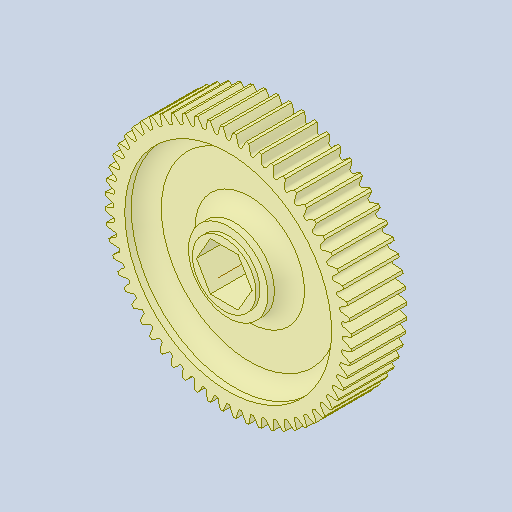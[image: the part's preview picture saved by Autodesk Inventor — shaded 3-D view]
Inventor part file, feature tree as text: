
AUTODESK INVENTOR PART (.ipt)
format: ipt  version: 2022.3 (Build 263350000, 350)  size: 659,968 bytes
history: native  units: in
note: dims shown in document units (in); Inventor stores cm internally (conversion verified against a paired STEP export)
features: mirror x1
ambient origin geometry x8: Origin, YZ Plane, XZ Plane, XY Plane, X Axis, Y Axis, Z Axis, Center Point
bodies: Solid1 (feature_tree)
feature tree (1):
  mirror  "Mirror1"
